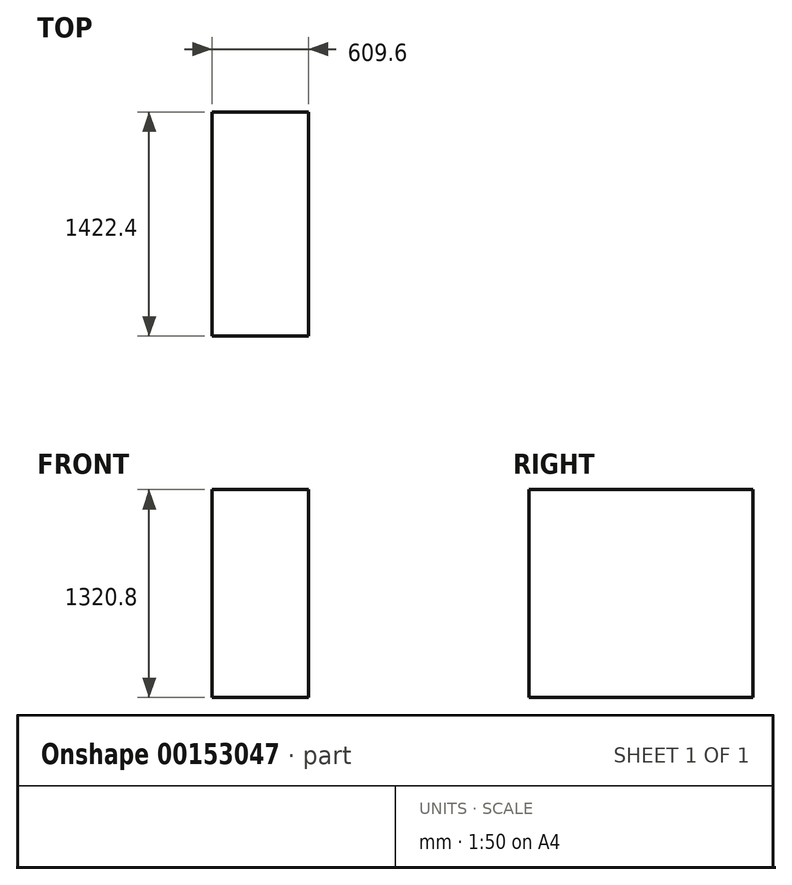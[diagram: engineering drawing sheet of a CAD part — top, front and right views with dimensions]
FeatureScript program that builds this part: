
annotation { "Feature Type Name" : "Feature", "Feature Type Description" : "" }
export const myFeature = defineFeature(function(context is Context, id is Id, definition is map)
    precondition{}
    {
        {
            var Q0;
            Q0=qCreatedBy(makeId("Top.planeOp"),FACE);
            var sketch = newSketch(context, id + "F0", { "sketchPlane" : qUnion([Q0])});
            skLineSegment(sketch, "E0.bottom", {"start": v(0, 0) * mm, "end": v(-609.6, 0) * mm});
            skLineSegment(sketch, "E0.top", {"start": v(0, -1422.4) * mm, "end": v(-609.6, -1422.4) * mm});
            skLineSegment(sketch, "E0.left", {"start": v(0, 0) * mm, "end": v(0, -1422.4) * mm});
            skLineSegment(sketch, "E0.right", {"start": v(-609.6, 0) * mm, "end": v(-609.6, -1422.4) * mm});
            skSolve(sketch);
        }
        {
            var Q0;
            Q0 = qSketchRegion(id + "F0", true);
            extrude(context, id + "F1", {"entities" : qUnion([Q0]), "depth" : 1320.8 * mm});
        }
    });
